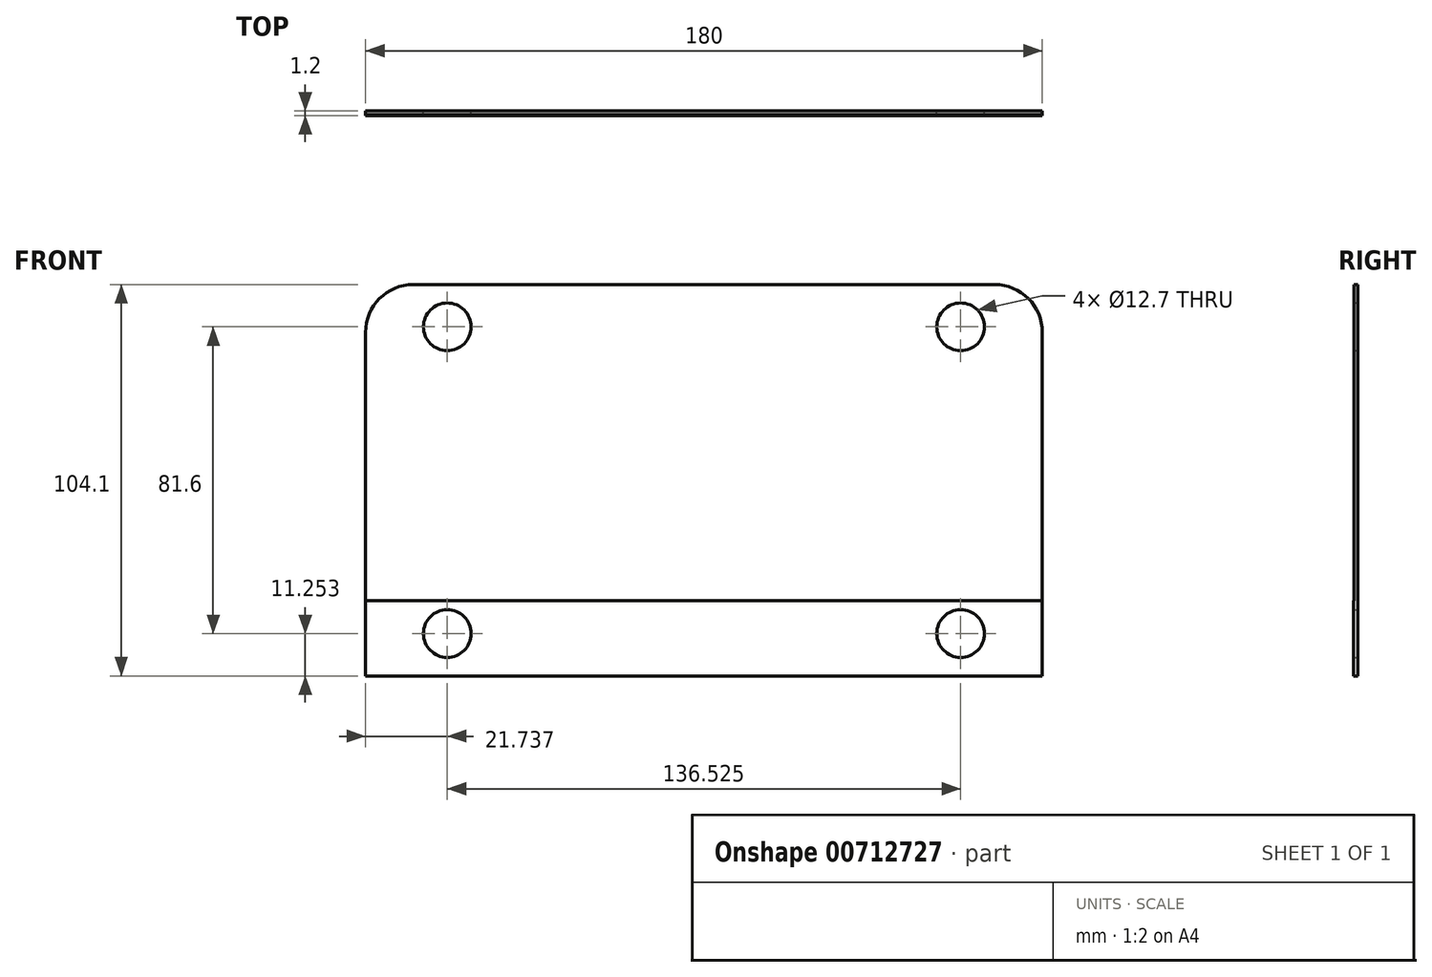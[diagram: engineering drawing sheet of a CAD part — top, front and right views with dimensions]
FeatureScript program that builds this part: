
annotation { "Feature Type Name" : "Feature", "Feature Type Description" : "" }
export const myFeature = defineFeature(function(context is Context, id is Id, definition is map)
    precondition{}
    {
        {
            var Q0;
            Q0=qCreatedBy(makeId("Front.planeOp"),FACE);
            var sketch = newSketch(context, id + "F0", { "sketchPlane" : qUnion([Q0])});
            skLineSegment(sketch, "E0", {"start": v(-77.3, 78) * mm, "end": v(77.3, 78) * mm});
            skLineSegment(sketch, "E1", {"start": v(-90, -26.1) * mm, "end": v(-90, 65.3) * mm});
            skLineSegment(sketch, "E2", {"start": v(90, 65.3) * mm, "end": v(90, -26.1) * mm});
            skCircle(sketch, "E3", {"center": v(-68.26, 66.75) * mm, "radius": 6.35 * mm});
            skCircle(sketch, "E4", {"center": v(68.26, 66.75) * mm, "radius": 6.35 * mm});
            skArc(sketch, "E5", {"start": v(-77.3, 78) * mm, "mid": v(-86.28, 74.28) * mm, "end": v(-90, 65.3) * mm});
            skArc(sketch, "E6", {"start": v(90, 65.3) * mm, "mid": v(86.28, 74.28) * mm, "end": v(77.3, 78) * mm});
            skLineSegment(sketch, "E7", {"start": v(-90, -26.1) * mm, "end": v(90, -26.1) * mm});
            skLineSegment(sketch, "E8", {"start": v(0, 78) * mm, "end": v(0, 44.35) * mm, "construction": true});
            skLineSegment(sketch, "E9", {"start": v(0, 0) * mm, "end": v(0, -26.1) * mm, "construction": true});
            skLineSegment(sketch, "E10", {"start": v(0, 44.35) * mm, "end": v(-90, 44.35) * mm, "construction": true});
            skLineSegment(sketch, "E11", {"start": v(0, 44.35) * mm, "end": v(90, 44.35) * mm, "construction": true});
            skCircle(sketch, "E12", {"center": v(-68.26, -14.85) * mm, "radius": 6.35 * mm});
            skCircle(sketch, "E13", {"center": v(68.26, -14.85) * mm, "radius": 6.35 * mm});
            skLineSegment(sketch, "E14", {"start": v(-68.26, 66.75) * mm, "end": v(-68.26, 78) * mm, "construction": true});
            skLineSegment(sketch, "E15", {"start": v(-68.26, -14.85) * mm, "end": v(-68.26, -26.1) * mm, "construction": true});
            skSolve(sketch);
        }
        {
            var Q0;
            Q0=qSketchRegion(id+"F0",true);
            extrude(context, id + "F1", {"entities" : qUnion([Q0]), "depth" : 1 * mm, "offsetDistance" : 25 * mm});
        }
        {
            var Q0;
            Q0=makeQuery(id+"F1.opExtrude","CAP_FACE",FACE,{"disambiguationData":[OSD([sQuery(id+"F0.wireOp",EDGE,"E0"),sQuery(id+"F0.wireOp",EDGE,"E1"),sQuery(id+"F0.wireOp",EDGE,"E2"),sQuery(id+"F0.wireOp",EDGE,"E3"),sQuery(id+"F0.wireOp",EDGE,"E4"),sQuery(id+"F0.wireOp",EDGE,"E5"),sQuery(id+"F0.wireOp",EDGE,"E6"),sQuery(id+"F0.wireOp",EDGE,"E7"),sQuery(id+"F0.wireOp",EDGE,"E12"),sQuery(id+"F0.wireOp",EDGE,"E13")])],"isStart":false});
            var sketch = newSketch(context, id + "F2", { "sketchPlane" : qUnion([Q0])});
            skLineSegment(sketch, "E16", {"start": v(-90, -26.1) * mm, "end": v(-90, -6.1) * mm});
            skLineSegment(sketch, "E17", {"start": v(-90, -6.1) * mm, "end": v(90, -6.1) * mm});
            skLineSegment(sketch, "E18", {"start": v(90, -6.1) * mm, "end": v(90, -26.1) * mm});
            skLineSegment(sketch, "E19", {"start": v(90, -26.1) * mm, "end": v(-90, -26.1) * mm});
            skCircle(sketch, "E20.0", {"center": v(-68.26, -14.85) * mm, "radius": 6.35 * mm});
            skCircle(sketch, "E21.0", {"center": v(68.26, -14.85) * mm, "radius": 6.35 * mm});
            skSolve(sketch);
        }
        {
            var Q0;
            Q0 = qSketchRegion(id + "F2", true);
            extrude(context, id + "F3", {"entities" : qUnion([Q0]), "operationType" : NewBodyOperationType.ADD, "depth" : .2 * mm, "offsetDistance" : 25 * mm});
        }
    });
